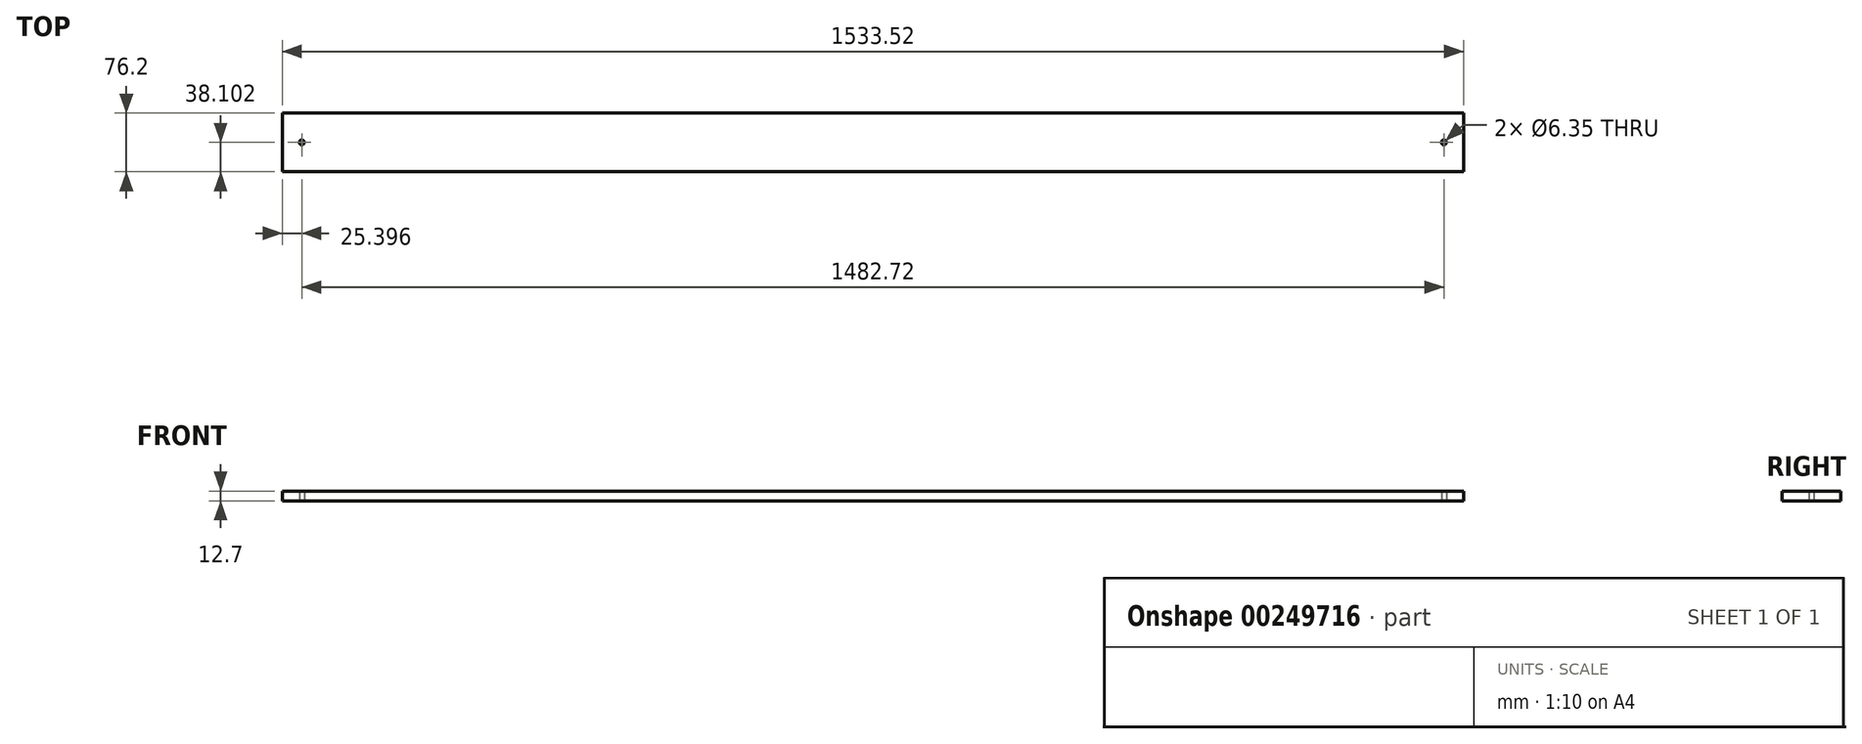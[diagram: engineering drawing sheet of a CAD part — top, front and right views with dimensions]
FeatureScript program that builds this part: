
annotation { "Feature Type Name" : "Feature", "Feature Type Description" : "" }
export const myFeature = defineFeature(function(context is Context, id is Id, definition is map)
    precondition{}
    {
        {
            var Q0;
            Q0=qCreatedBy(makeId("Top.planeOp"),FACE);
            var sketch = newSketch(context, id + "F0", { "sketchPlane" : qUnion([Q0])});
            skLineSegment(sketch, "E0.bottom", {"start": v(-932.78, 57.53) * mm, "end": v(600.74, 57.53) * mm});
            skLineSegment(sketch, "E0.top", {"start": v(-932.78, -18.67) * mm, "end": v(600.74, -18.67) * mm});
            skLineSegment(sketch, "E0.left", {"start": v(-932.78, 57.53) * mm, "end": v(-932.78, -18.67) * mm});
            skLineSegment(sketch, "E0.right", {"start": v(600.74, 57.53) * mm, "end": v(600.74, -18.67) * mm});
            skCircle(sketch, "E1", {"center": v(-907.38, 19.43) * mm, "radius": 3.18 * mm});
            skLineSegment(sketch, "E2", {"start": v(-932.78, 19.43) * mm, "end": v(-859.79, 19.43) * mm, "construction": true});
            skLineSegment(sketch, "E3", {"start": v(600.74, 19.43) * mm, "end": v(481.3, 19.43) * mm, "construction": true});
            skCircle(sketch, "E4", {"center": v(575.34, 19.43) * mm, "radius": 3.18 * mm});
            skSolve(sketch);
        }
        {
            var Q0;
            Q0=makeQuery(id+"F0.imprint","IMPRINT",FACE,{"disambiguationData":[TD([[makeQuery(id+"F0.imprint","IMPRINT",EDGE,{"derivedFrom":sQuery(id+"F0.wireOp",EDGE,"E0.bottom")}),-1.0]])]});
            extrude(context, id + "F1", {"entities" : qUnion([Q0]), "depth" : 12.7 * mm});
        }
    });
